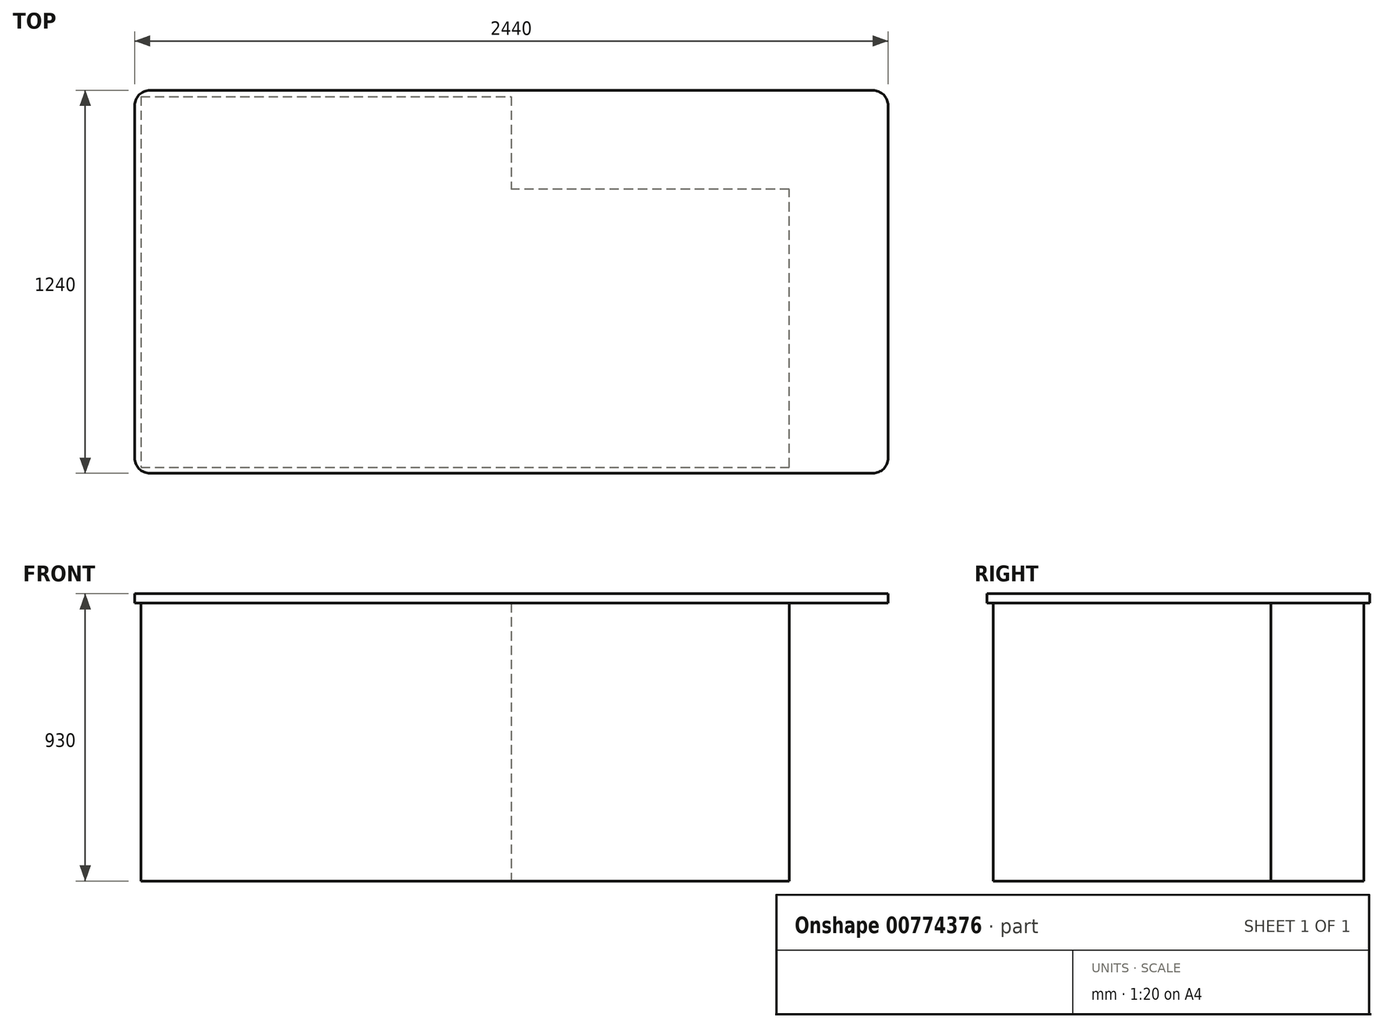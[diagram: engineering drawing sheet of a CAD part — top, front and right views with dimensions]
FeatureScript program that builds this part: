
annotation { "Feature Type Name" : "Feature", "Feature Type Description" : "" }
export const myFeature = defineFeature(function(context is Context, id is Id, definition is map)
    precondition{}
    {
        {
            var Q0;
            Q0=qCreatedBy(makeId("Top.planeOp"),FACE);
            var sketch = newSketch(context, id + "F0", { "sketchPlane" : qUnion([Q0])});
            skLineSegment(sketch, "E0.bottom", {"start": v(-1188.21, 434.47) * mm, "end": v(1211.79, 434.47) * mm});
            skLineSegment(sketch, "E0.top", {"start": v(-1188.21, -765.53) * mm, "end": v(1211.79, -765.53) * mm});
            skLineSegment(sketch, "E0.left", {"start": v(-1188.21, 434.47) * mm, "end": v(-1188.21, -765.53) * mm});
            skLineSegment(sketch, "E0.right", {"start": v(1211.79, 434.47) * mm, "end": v(1211.79, -765.53) * mm});
            skSolve(sketch);
        }
        {
            var Q0;
            Q0 = qSketchRegion(id + "F0", true);
            extrude(context, id + "F1", {"entities" : qUnion([Q0]), "depth" : 900 * mm, "offsetDistance" : 25 * mm});
        }
        {
            var Q0;
            Q0=makeQuery(id+"F1.opExtrude","CAP_FACE",FACE,{"disambiguationData":[OSD([sQuery(id+"F0.wireOp",EDGE,"E0.bottom"),sQuery(id+"F0.wireOp",EDGE,"E0.top"),sQuery(id+"F0.wireOp",EDGE,"E0.left"),sQuery(id+"F0.wireOp",EDGE,"E0.right")])],"isStart":false});
            var sketch = newSketch(context, id + "F2", { "sketchPlane" : qUnion([Q0])});
            skLineSegment(sketch, "E1.bottom", {"start": v(1231.79, -785.53) * mm, "end": v(-1208.21, -785.53) * mm});
            skLineSegment(sketch, "E1.top", {"start": v(1231.79, 454.47) * mm, "end": v(-1208.21, 454.47) * mm});
            skLineSegment(sketch, "E1.left", {"start": v(1231.79, -785.53) * mm, "end": v(1231.79, 454.47) * mm});
            skLineSegment(sketch, "E1.right", {"start": v(-1208.21, -785.53) * mm, "end": v(-1208.21, 454.47) * mm});
            skSolve(sketch);
        }
        {
            var Q0;
            Q0 = qSketchRegion(id + "F2", true);
            extrude(context, id + "F3", {"entities" : qUnion([Q0]), "operationType" : NewBodyOperationType.ADD, "depth" : 30 * mm, "offsetDistance" : 25 * mm});
        }
        {
            var Q0;
            Q0=makeQuery(id+"F1.opExtrude","CAP_FACE",FACE,{"disambiguationData":[OSD([sQuery(id+"F0.wireOp",EDGE,"E0.bottom"),sQuery(id+"F0.wireOp",EDGE,"E0.top"),sQuery(id+"F0.wireOp",EDGE,"E0.left"),sQuery(id+"F0.wireOp",EDGE,"E0.right")])],"isStart":true});
            var sketch = newSketch(context, id + "F4", { "sketchPlane" : qUnion([Q0])});
            skLineSegment(sketch, "E2.bottom", {"start": v(1211.79, -434.47) * mm, "end": v(11.79, -434.47) * mm});
            skLineSegment(sketch, "E2.top", {"start": v(1211.79, -134.47) * mm, "end": v(11.79, -134.47) * mm});
            skLineSegment(sketch, "E2.left", {"start": v(1211.79, -434.47) * mm, "end": v(1211.79, -134.47) * mm});
            skLineSegment(sketch, "E2.right", {"start": v(11.79, -434.47) * mm, "end": v(11.79, -134.47) * mm});
            skLineSegment(sketch, "E3.bottom", {"start": v(1211.79, 765.53) * mm, "end": v(911.79, 765.53) * mm});
            skLineSegment(sketch, "E3.top", {"start": v(1211.79, -434.47) * mm, "end": v(911.79, -434.47) * mm});
            skLineSegment(sketch, "E3.left", {"start": v(1211.79, 765.53) * mm, "end": v(1211.79, -434.47) * mm});
            skLineSegment(sketch, "E3.right", {"start": v(911.79, 765.53) * mm, "end": v(911.79, -434.47) * mm});
            skSolve(sketch);
        }
        {
            var Q0;
            Q0 = qSketchRegion(id + "F4", true);
            extrude(context, id + "F5", {"entities" : qUnion([Q0]), "operationType" : NewBodyOperationType.REMOVE, "oppositeDirection" : true, "depth" : 900 * mm, "offsetDistance" : 25 * mm});
        }
        {
            var Q0;
            Q0=makeQuery(id+"F3.opExtrude","SWEPT_EDGE",EDGE,{"disambiguationData":[OSD([sQuery(id+"F2.wireOp",EDGE,"E1.top"),sQuery(id+"F2.wireOp",EDGE,"E1.left")])]});
            var Q1;
            Q1=makeQuery(id+"F3.opExtrude","SWEPT_EDGE",EDGE,{"disambiguationData":[OSD([sQuery(id+"F2.wireOp",EDGE,"E1.bottom"),sQuery(id+"F2.wireOp",EDGE,"E1.left")])]});
            var Q2;
            Q2=makeQuery(id+"F3.opExtrude","SWEPT_EDGE",EDGE,{"disambiguationData":[OSD([sQuery(id+"F2.wireOp",EDGE,"E1.top"),sQuery(id+"F2.wireOp",EDGE,"E1.right")])]});
            var Q3;
            Q3=makeQuery(id+"F3.opExtrude","SWEPT_EDGE",EDGE,{"disambiguationData":[OSD([sQuery(id+"F2.wireOp",EDGE,"E1.bottom"),sQuery(id+"F2.wireOp",EDGE,"E1.right")])]});
            fillet(context, id + "F6", {"entities" : qUnion([Q0, Q1, Q2, Q3]), "radius" : 50 * mm, "tangentPropagation" : true, "allowEdgeOverflow" : false});
        }
    });
